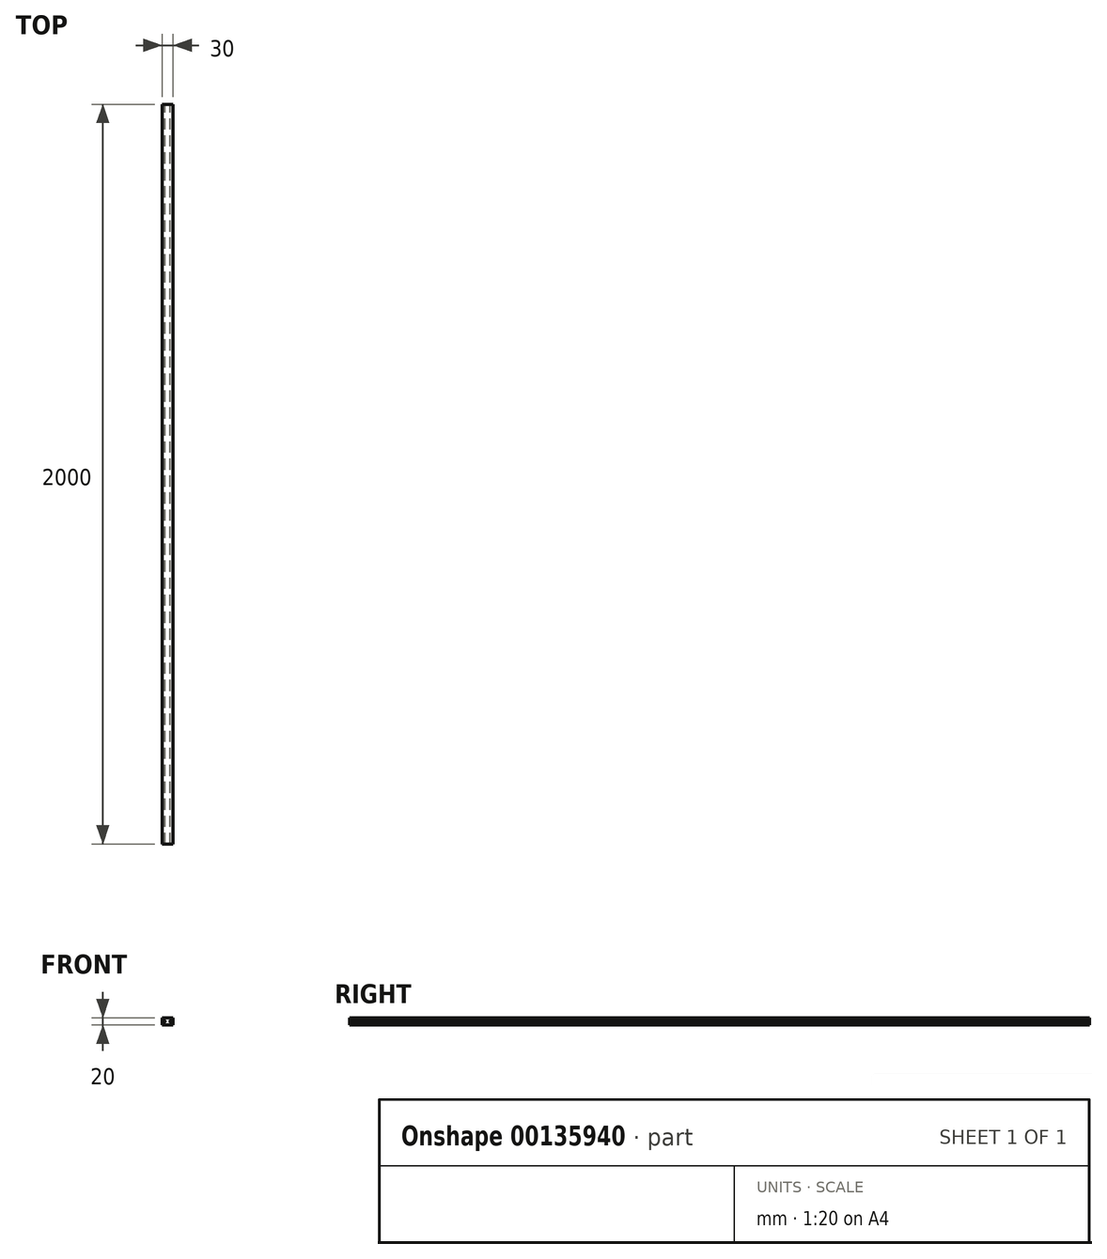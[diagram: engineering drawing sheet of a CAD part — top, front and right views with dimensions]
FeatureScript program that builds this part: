
annotation { "Feature Type Name" : "Feature", "Feature Type Description" : "" }
export const myFeature = defineFeature(function(context is Context, id is Id, definition is map)
    precondition{}
    {
        {
            var Q0;
            Q0=qCreatedBy(makeId("Front.planeOp"),FACE);
            var sketch = newSketch(context, id + "F0", { "sketchPlane" : qUnion([Q0])});
            skLineSegment(sketch, "E0.bottom", {"start": v(15, 10) * mm, "end": v(-15, 10) * mm});
            skLineSegment(sketch, "E0.top", {"start": v(15, -10) * mm, "end": v(-15, -10) * mm});
            skLineSegment(sketch, "E0.left", {"start": v(15, 10) * mm, "end": v(15, 1) * mm});
            skLineSegment(sketch, "E0.right", {"start": v(-15, 10) * mm, "end": v(-15, 1) * mm});
            skPoint(sketch, "E0.middle", {"position": v(0, 0) * mm});
            skArc(sketch, "E1", {"start": v(-14.6, -0.95) * mm, "mid": v(-6.72, 0) * mm, "end": v(-14.6, 0.95) * mm});
            skArc(sketch, "E2.filletArc", {"start": v(-15, 1) * mm, "mid": v(-14.82, 0.8) * mm, "end": v(-14.6, 0.95) * mm});
            skLineSegment(sketch, "E3", {"start": v(-15, -10) * mm, "end": v(-15, -1) * mm});
            skArc(sketch, "E4.filletArc", {"start": v(-14.6, -0.95) * mm, "mid": v(-14.82, -0.8) * mm, "end": v(-15, -1) * mm});
            skLineSegment(sketch, "E5", {"start": v(0, 0) * mm, "end": v(0, 5.83) * mm});
            skArc(sketch, "E6.MirrorCS", {"start": v(14.6, -0.95) * mm, "mid": v(6.72, 0) * mm, "end": v(14.6, 0.95) * mm});
            skArc(sketch, "E7.MirrorCS", {"start": v(15, 1) * mm, "mid": v(14.82, 0.8) * mm, "end": v(14.6, 0.95) * mm});
            skArc(sketch, "E8.MirrorCS", {"start": v(14.6, -0.95) * mm, "mid": v(14.82, -0.8) * mm, "end": v(15, -1) * mm});
            skLineSegment(sketch, "E9.trimOffspring", {"start": v(15, -1) * mm, "end": v(15, -10) * mm});
            skSolve(sketch);
        }
        {
            var Q0;
            Q0=makeQuery(id+"F0.imprint","IMPRINT",FACE,{"disambiguationData":[TD([[makeQuery(id+"F0.imprint","IMPRINT",EDGE,{"derivedFrom":sQuery(id+"F0.wireOp",EDGE,"E0.bottom")}),1.0]])]});
            extrude(context, id + "F1", {"entities" : qUnion([Q0]), "endBound" : BoundingType.SYMMETRIC, "depth" : 2000 * mm});
        }
    });
